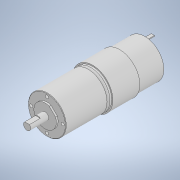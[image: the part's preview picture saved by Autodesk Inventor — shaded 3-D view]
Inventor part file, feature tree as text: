
AUTODESK INVENTOR PART (.ipt)
format: ipt  version: 2021 (Build 250183000, 183)  size: 198,656 bytes
history: native  units: mm
features: extrude x9, sketch x9, other x1, fillet x1, chamfer x1
ambient origin geometry x8: Origin, YZ Plane, XZ Plane, XY Plane, X Axis, Y Axis, Z Axis, Center Point
bodies: Body1 (feature_tree)
feature tree (21):
  other  "ソリッド1"
  extrude  "押し出し1"  Depth=42.4mm
  extrude  "押し出し2"  Depth=5.0mm TaperAngle=0.0deg
  extrude  "押し出し3"  Depth=45.0mm
  fillet  "フィレット1"  Radius=30.0mm
  extrude  "押し出し4"  Depth=42.4mm
  extrude  "押し出し5"  Depth=28.0mm TaperAngle=0.0deg
  chamfer  "面取り1"  Distance=3.0mm
  extrude  "押し出し6"  Depth=3.5mm
  extrude  "押し出し7"  Depth=1.0mm
  extrude  "押し出し8"  Depth=3.5mm
  extrude  "押し出し9"  Depth=1.0mm
  sketch  "スケッチ1"
  sketch  "スケッチ2"
  sketch  "スケッチ3"
  sketch  "スケッチ4"
  sketch  "スケッチ5"
  sketch  "スケッチ6"
  sketch  "スケッチ7"
  sketch  "スケッチ8"
  sketch  "スケッチ9"
